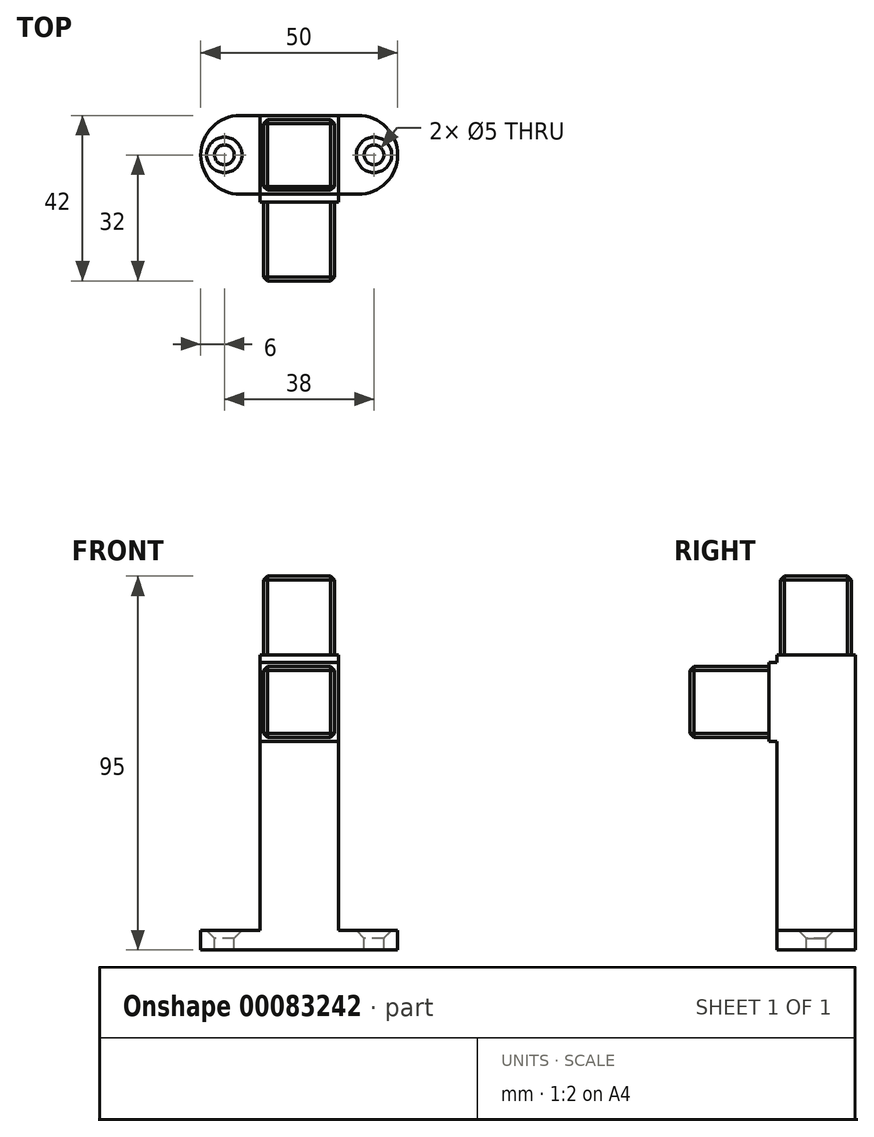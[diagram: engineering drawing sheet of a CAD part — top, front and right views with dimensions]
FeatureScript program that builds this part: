
annotation { "Feature Type Name" : "Feature", "Feature Type Description" : "" }
export const myFeature = defineFeature(function(context is Context, id is Id, definition is map)
    precondition{}
    {
        {
            var Q0;
            Q0=qCreatedBy(makeId("Top.planeOp"),FACE);
            var sketch = newSketch(context, id + "F0", { "sketchPlane" : qUnion([Q0])});
            skLineSegment(sketch, "E0.bottom", {"start": v(0, 0) * mm, "end": v(30, 0) * mm});
            skLineSegment(sketch, "E0.top", {"start": v(0, 20) * mm, "end": v(30, 20) * mm});
            skLineSegment(sketch, "E0.left", {"start": v(0, 0) * mm, "end": v(0, 20) * mm});
            skLineSegment(sketch, "E0.right", {"start": v(30, 0) * mm, "end": v(30, 20) * mm});
            skArc(sketch, "E1", {"start": v(0, 20) * mm, "mid": v(-10, 10) * mm, "end": v(0, 0) * mm});
            skArc(sketch, "E2", {"start": v(30, 0) * mm, "mid": v(40, 10) * mm, "end": v(30, 20) * mm});
            skLineSegment(sketch, "E3", {"start": v(5, 20) * mm, "end": v(5, 0) * mm});
            skLineSegment(sketch, "E4", {"start": v(25, 20) * mm, "end": v(25, 0) * mm});
            skCircle(sketch, "E5", {"center": v(34, 10) * mm, "radius": 2.5 * mm});
            skCircle(sketch, "E6", {"center": v(-4, 10) * mm, "radius": 2.5 * mm});
            skSolve(sketch);
        }
        {
            var Q0;
            {var subQ1=sQuery(id+"F0.wireOp",EDGE,"E3");Q0=makeQuery(id+"F0.imprint","IMPRINT",FACE,{"disambiguationData":[TD([[makeQuery(id+"F0.imprint","IMPRINT",EDGE,{"derivedFrom":subQ1}),1.0]])]});}
            extrude(context, id + "F1", {"entities" : qUnion([Q0]), "depth" : 70 * mm});
        }
        {
            var Q0;
            Q0=qSketchRegion(id+"F0",true);
            extrude(context, id + "F2", {"entities" : qUnion([Q0]), "operationType" : NewBodyOperationType.ADD, "oppositeDirection" : true, "depth" : 5 * mm});
        }
        {
            var Q0;
            Q0=makeQuery(id+"F1.opExtrude","CAP_FACE",FACE,{"disambiguationData":[OSD([sQuery(id+"F0.wireOp",EDGE,"E0.bottom"),sQuery(id+"F0.wireOp",EDGE,"E0.top"),sQuery(id+"F0.wireOp",EDGE,"E3"),sQuery(id+"F0.wireOp",EDGE,"E4")])],"isStart":false});
            var sketch = newSketch(context, id + "F3", { "sketchPlane" : qUnion([Q0])});
            skLineSegment(sketch, "E7", {"start": v(6, 19) * mm, "end": v(24, 19) * mm});
            skLineSegment(sketch, "E8", {"start": v(24, 19) * mm, "end": v(24, 1) * mm});
            skLineSegment(sketch, "E9", {"start": v(6, 19) * mm, "end": v(6, 1) * mm});
            skLineSegment(sketch, "E10", {"start": v(6, 1) * mm, "end": v(24, 1) * mm});
            skSolve(sketch);
        }
        {
            var Q0;
            Q0=makeQuery(id+"F3.imprint","IMPRINT",FACE,{"disambiguationData":[TD([[makeQuery(id+"F3.imprint","IMPRINT",EDGE,{"derivedFrom":sQuery(id+"F3.wireOp",EDGE,"E7")}),-1.0]])]});
            extrude(context, id + "F4", {"entities" : qUnion([Q0]), "operationType" : NewBodyOperationType.ADD, "depth" : 20 * mm});
        }
        {
            var Q0;
            {var subQ0=sQuery(id+"F0.wireOp",EDGE,"E0.bottom");Q0=makeQuery(id+"F2.boolean.opBoolean","MERGE",FACE,{"derivedFrom":[makeQuery(id+"F1.opExtrude","SWEPT_FACE",FACE,{"disambiguationData":[OSD([subQ0])]}),makeQuery(id+"F2.opExtrude","SWEPT_FACE",FACE,{"disambiguationData":[OSD([subQ0])]})]});}
            var sketch = newSketch(context, id + "F5", { "sketchPlane" : qUnion([Q0])});
            skLineSegment(sketch, "E11", {"start": v(5, 68) * mm, "end": v(25, 68) * mm});
            skLineSegment(sketch, "E12", {"start": v(25, 68) * mm, "end": v(25, 48) * mm});
            skLineSegment(sketch, "E13", {"start": v(25, 48) * mm, "end": v(5, 48) * mm});
            skLineSegment(sketch, "E14", {"start": v(5, 48) * mm, "end": v(5, 68) * mm});
            skSolve(sketch);
        }
        {
            var Q0;
            Q0=makeQuery(id+"F5.imprint","IMPRINT",FACE,{"disambiguationData":[TD([[makeQuery(id+"F5.imprint","IMPRINT",EDGE,{"derivedFrom":sQuery(id+"F5.wireOp",EDGE,"E11")}),-1.0]])]});
            extrude(context, id + "F6", {"entities" : qUnion([Q0]), "operationType" : NewBodyOperationType.ADD, "depth" : 2 * mm});
        }
        {
            var Q0;
            Q0=makeQuery(id+"F2.opExtrude","CAP_EDGE",EDGE,{"disambiguationData":[OSD([sQuery(id+"F0.wireOp",EDGE,"E5")])],"isStart":true});
            var Q1;
            Q1=makeQuery(id+"F2.opExtrude","CAP_EDGE",EDGE,{"disambiguationData":[OSD([sQuery(id+"F0.wireOp",EDGE,"E6")])],"isStart":true});
            chamfer(context, id + "F7", {"entities" : qUnion([Q0, Q1]), "width" : 2 * mm, "tangentPropagation" : true});
        }
        {
            var Q0;
            Q0=makeQuery(id+"F4.opExtrude","SWEPT_EDGE",EDGE,{"disambiguationData":[OSD([sQuery(id+"F3.wireOp",EDGE,"E7"),sQuery(id+"F3.wireOp",EDGE,"E8")])]});
            var Q1;
            Q1=makeQuery(id+"F4.opExtrude","SWEPT_EDGE",EDGE,{"disambiguationData":[OSD([sQuery(id+"F3.wireOp",EDGE,"E7"),sQuery(id+"F3.wireOp",EDGE,"E9")])]});
            var Q2;
            Q2=makeQuery(id+"F4.opExtrude","CAP_EDGE",EDGE,{"disambiguationData":[OSD([sQuery(id+"F3.wireOp",EDGE,"E7")])],"isStart":false});
            var Q3;
            Q3=makeQuery(id+"F4.opExtrude","CAP_EDGE",EDGE,{"disambiguationData":[OSD([sQuery(id+"F3.wireOp",EDGE,"E9")])],"isStart":false});
            var Q4;
            Q4=makeQuery(id+"F4.opExtrude","CAP_EDGE",EDGE,{"disambiguationData":[OSD([sQuery(id+"F3.wireOp",EDGE,"E8")])],"isStart":false});
            var Q5;
            Q5=makeQuery(id+"F4.opExtrude","CAP_EDGE",EDGE,{"disambiguationData":[OSD([sQuery(id+"F3.wireOp",EDGE,"E10")])],"isStart":false});
            var Q6;
            Q6=makeQuery(id+"F4.opExtrude","SWEPT_EDGE",EDGE,{"disambiguationData":[OSD([sQuery(id+"F3.wireOp",EDGE,"E8"),sQuery(id+"F3.wireOp",EDGE,"E10")])]});
            var Q7;
            Q7=makeQuery(id+"F4.opExtrude","SWEPT_EDGE",EDGE,{"disambiguationData":[OSD([sQuery(id+"F3.wireOp",EDGE,"E9"),sQuery(id+"F3.wireOp",EDGE,"E10")])]});
            chamfer(context, id + "F8", {"entities" : qUnion([Q0, Q1, Q2, Q3, Q4, Q5, Q6, Q7]), "width" : 1 * mm, "tangentPropagation" : true});
        }
        {
            var Q0;
            Q0=makeQuery(id+"F6.opExtrude","CAP_FACE",FACE,{"disambiguationData":[OSD([sQuery(id+"F5.wireOp",EDGE,"E11"),sQuery(id+"F5.wireOp",EDGE,"E12"),sQuery(id+"F5.wireOp",EDGE,"E13"),sQuery(id+"F5.wireOp",EDGE,"E14")])],"isStart":false});
            var sketch = newSketch(context, id + "F9", { "sketchPlane" : qUnion([Q0])});
            skLineSegment(sketch, "E15", {"start": v(6, 67) * mm, "end": v(24, 67) * mm});
            skLineSegment(sketch, "E16", {"start": v(24, 67) * mm, "end": v(24, 49) * mm});
            skLineSegment(sketch, "E17", {"start": v(24, 49) * mm, "end": v(6, 49) * mm});
            skLineSegment(sketch, "E18", {"start": v(6, 49) * mm, "end": v(6, 67) * mm});
            skSolve(sketch);
        }
        {
            var Q0;
            Q0=makeQuery(id+"F9.imprint","IMPRINT",FACE,{"disambiguationData":[TD([[makeQuery(id+"F9.imprint","IMPRINT",EDGE,{"derivedFrom":sQuery(id+"F9.wireOp",EDGE,"E15")}),-1.0]])]});
            extrude(context, id + "F10", {"entities" : qUnion([Q0]), "operationType" : NewBodyOperationType.ADD, "depth" : 20 * mm});
        }
        {
            var Q0;
            Q0=makeQuery(id+"F10.opExtrude","SWEPT_EDGE",EDGE,{"disambiguationData":[OSD([sQuery(id+"F9.wireOp",EDGE,"E15"),sQuery(id+"F9.wireOp",EDGE,"E16")])]});
            var Q1;
            Q1=makeQuery(id+"F10.opExtrude","CAP_EDGE",EDGE,{"disambiguationData":[OSD([sQuery(id+"F9.wireOp",EDGE,"E15")])],"isStart":false});
            var Q2;
            Q2=makeQuery(id+"F10.opExtrude","SWEPT_EDGE",EDGE,{"disambiguationData":[OSD([sQuery(id+"F9.wireOp",EDGE,"E15"),sQuery(id+"F9.wireOp",EDGE,"E18")])]});
            var Q3;
            Q3=makeQuery(id+"F10.opExtrude","CAP_EDGE",EDGE,{"disambiguationData":[OSD([sQuery(id+"F9.wireOp",EDGE,"E16")])],"isStart":false});
            var Q4;
            Q4=makeQuery(id+"F10.opExtrude","SWEPT_EDGE",EDGE,{"disambiguationData":[OSD([sQuery(id+"F9.wireOp",EDGE,"E16"),sQuery(id+"F9.wireOp",EDGE,"E17")])]});
            var Q5;
            Q5=makeQuery(id+"F10.opExtrude","SWEPT_EDGE",EDGE,{"disambiguationData":[OSD([sQuery(id+"F9.wireOp",EDGE,"E17"),sQuery(id+"F9.wireOp",EDGE,"E18")])]});
            var Q6;
            Q6=makeQuery(id+"F10.opExtrude","CAP_EDGE",EDGE,{"disambiguationData":[OSD([sQuery(id+"F9.wireOp",EDGE,"E18")])],"isStart":false});
            var Q7;
            Q7=makeQuery(id+"F10.opExtrude","CAP_EDGE",EDGE,{"disambiguationData":[OSD([sQuery(id+"F9.wireOp",EDGE,"E17")])],"isStart":false});
            chamfer(context, id + "F11", {"entities" : qUnion([Q0, Q1, Q2, Q3, Q4, Q5, Q6, Q7]), "width" : 1 * mm, "tangentPropagation" : true});
        }
    });
